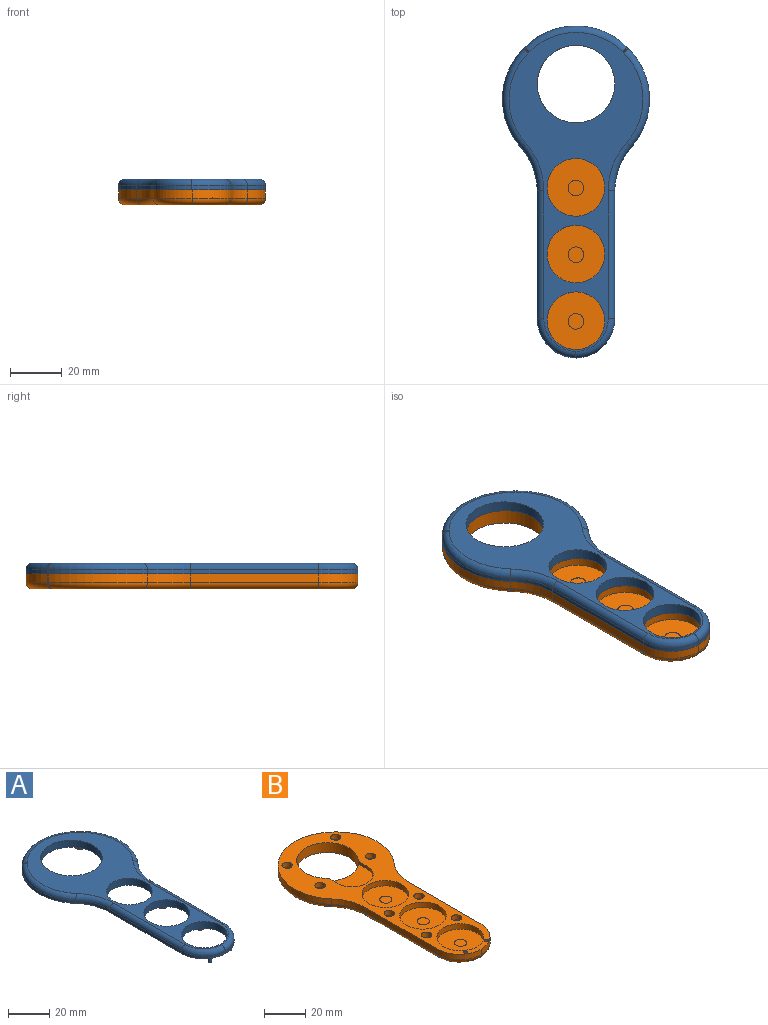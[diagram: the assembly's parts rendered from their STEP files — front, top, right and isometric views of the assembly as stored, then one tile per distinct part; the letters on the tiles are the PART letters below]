
ASSEMBLY  parts=2 mates=1
PART A: 48 faces, bbox 61.5x132x7.2 mm
  f0: plane 1.64x0.49mm, normal (0.71,0.71,0), area 1.1mm2, adj f5,f6,f8,f40
  f1: plane 1.64x0.49mm, normal (-0.71,0.71,0), area 1.1mm2, adj f5,f6,f7,f37
  f2: plane 49.38x1.64mm, normal (-1,0,0), area 80.7mm2, adj f5,f9,f12,f43
  f3: plane 49.38x1.64mm, normal (1,0,0), area 80.7mm2, adj f5,f10,f11,f46
  f4: plane 123.34x51.77mm, normal (0,0,1), area 1996.3mm2, adj f13,f14,f15,f16,f37,f38,f39,f40
  f5: plane 128.43x56.85mm, normal (0,0,-1), area 2639.4mm2, adj f0,f1,f2,f3,f6,f7,f8,f9
  f6: cylinder r=27.94mm len=39.51mm, axis (0,0,-1), area 71.8mm2, adj f0,f1,f5,f38
  f7: cylinder r=27.94mm len=38.29mm, axis (0,0,-1), area 69mm2, adj f1,f5,f9,f39
  f8: cylinder r=27.94mm len=38.29mm, axis (0,0,-1), area 69mm2, adj f0,f5,f10,f42
  f9: cylinder r=25.4mm len=16.85mm, axis (0,0,-1), area 30.1mm2, adj f2,f5,f7,f41
  f10: cylinder r=25.4mm len=16.85mm, axis (0,0,-1), area 30.1mm2, adj f3,f5,f8,f44
  f11: cylinder r=15.24mm len=15.24mm, axis (0,0,-1), area 38.7mm2, adj f3,f5,f12,f47
  f12: cylinder r=15.24mm len=15.24mm, axis (0,0,-1), area 38.7mm2, adj f2,f5,f11,f45
  f13: cylinder r=15mm len=30mm, axis (0,0,1), area 393.5mm2, adj f4,f5
  f14: cylinder r=11.15mm len=22.3mm, axis (0,0,1), area 292.5mm2, adj f4,f5
  f15: cylinder r=11.15mm len=22.3mm, axis (0,0,1), area 292.5mm2, adj f4,f5
  f16: cylinder r=11.15mm len=22.3mm, axis (0,0,1), area 292.5mm2, adj f4,f5
  f17: cylinder r=2.25mm len=4.5mm, axis (0,0,1), area 42.4mm2, adj f5,f18
  f18: plane 4.5x4.5mm, normal (0,0,-1), area 15.9mm2, adj f17
  f19: cylinder r=2.25mm len=4.5mm, axis (0,0,1), area 42.4mm2, adj f5,f20
  f20: plane 4.5x4.5mm, normal (0,0,-1), area 15.9mm2, adj f19
  f21: cylinder r=2.25mm len=4.5mm, axis (0,0,1), area 42.4mm2, adj f5,f22
  f22: plane 4.5x4.5mm, normal (0,0,-1), area 15.9mm2, adj f21
  f23: cylinder r=2.25mm len=4.5mm, axis (0,0,1), area 42.4mm2, adj f5,f24
  f24: plane 4.5x4.5mm, normal (0,0,-1), area 15.9mm2, adj f23
  f25: cylinder r=2.25mm len=4.5mm, axis (0,0,1), area 42.4mm2, adj f5,f26
  f26: plane 4.5x4.5mm, normal (0,0,-1), area 15.9mm2, adj f25
  f27: cylinder r=2.25mm len=4.5mm, axis (0,0,1), area 42.4mm2, adj f5,f28
  f28: plane 4.5x4.5mm, normal (0,0,-1), area 15.9mm2, adj f27
  f29: cylinder r=2.25mm len=4.5mm, axis (0,0,1), area 42.4mm2, adj f5,f30
  f30: plane 4.5x4.5mm, normal (0,0,-1), area 15.9mm2, adj f29
  f31: cylinder r=2.25mm len=4.5mm, axis (0,0,1), area 42.4mm2, adj f5,f32
  f32: plane 4.5x4.5mm, normal (0,0,-1), area 15.9mm2, adj f31
  f33: cylinder r=0.75mm len=3mm, axis (0,0,1), area 14.1mm2, adj f5,f34
  f34: plane 1.5x1.5mm, normal (0,0,-1), area 1.8mm2, adj f33
  f35: cylinder r=0.75mm len=3mm, axis (0,0,1), area 14.1mm2, adj f5,f36
  f36: plane 1.5x1.5mm, normal (0,0,-1), area 1.8mm2, adj f35
  f37: cylinder r=2.54mm len=2.54mm, axis (0.71,0.71,0), area 2.7mm2, adj f1,f4,f38,f39
  f38: torus R=25.4mm, axis (0,0,1), area 169.3mm2, adj f4,f6,f37,f40
  f39: torus R=25.4mm, axis (0,0,1), area 162.8mm2, adj f4,f7,f37,f41
  f40: cylinder r=2.54mm len=2.54mm, axis (0.71,-0.71,0), area 2.7mm2, adj f0,f4,f38,f42
  f41: torus R=27.94mm, axis (0,0,1), area 76.2mm2, adj f4,f9,f39,f43
  f42: torus R=25.4mm, axis (0,0,1), area 162.8mm2, adj f4,f8,f40,f44
  f43: cylinder r=2.54mm len=49.38mm, axis (0,1,0), area 197mm2, adj f2,f4,f41,f45
  f44: torus R=27.94mm, axis (0,0,1), area 76.2mm2, adj f4,f10,f42,f46
  f45: torus R=12.7mm, axis (0,0,1), area 88.7mm2, adj f4,f12,f43,f47
  f46: cylinder r=2.54mm len=49.38mm, axis (0,-1,0), area 197mm2, adj f3,f4,f44,f47
  f47: torus R=12.7mm, axis (0,0,1), area 88.7mm2, adj f4,f11,f45,f46
PART B: 63 faces, bbox 61.5x132x5.8 mm
  f0: cylinder r=15mm len=30mm, axis (0,0,1), area 512.2mm2, adj f1,f6,f26,f28,f29
  f1: plane 128.43x56.85mm, normal (0,0,1), area 2326.2mm2, adj f0,f2,f3,f4,f5,f7,f8,f9
  f2: plane 3.29x0.49mm, normal (0.71,0.71,0), area 2.3mm2, adj f1,f7,f9,f58
  f3: plane 3.29x0.49mm, normal (-0.71,0.71,0), area 2.3mm2, adj f1,f7,f8,f62
  f4: plane 49.38x3.29mm, normal (-1,0,0), area 162.2mm2, adj f1,f10,f13,f57
  f5: plane 49.38x3.29mm, normal (1,0,0), area 162.2mm2, adj f1,f11,f12,f52
  f6: plane 123.34x51.77mm, normal (0,0,-1), area 3168mm2, adj f0,f52,f53,f54,f55,f56,f57,f58
  f7: cylinder r=27.94mm len=39.51mm, axis (0,0,-1), area 144.2mm2, adj f1,f2,f3,f60
  f8: cylinder r=27.94mm len=38.29mm, axis (0,0,-1), area 138.7mm2, adj f1,f3,f10,f61
  f9: cylinder r=27.94mm len=38.29mm, axis (0,0,-1), area 138.7mm2, adj f1,f2,f11,f56
  f10: cylinder r=25.4mm len=16.85mm, axis (0,0,-1), area 60.5mm2, adj f1,f4,f8,f59
  f11: cylinder r=25.4mm len=16.85mm, axis (0,0,-1), area 60.5mm2, adj f1,f5,f9,f54
  f12: cylinder r=15.24mm len=15.24mm, axis (0,0,-1), area 77.9mm2, adj f1,f5,f13,f53
  f13: cylinder r=15.24mm len=15.24mm, axis (0,0,-1), area 77.9mm2, adj f1,f4,f12,f55
  f14: cylinder r=11.4mm len=22.8mm, axis (0,0,1), area 231mm2, adj f1,f15
  f15: plane 22.8x22.8mm, normal (0,0,1), area 380mm2, adj f14,f24
  f16: cylinder r=11.4mm len=22.8mm, axis (0,0,1), area 231mm2, adj f1,f17
  f17: plane 22.8x22.8mm, normal (0,0,1), area 380mm2, adj f16,f22
  f18: cylinder r=11.4mm len=22.8mm, axis (0,0,1), area 231mm2, adj f1,f19
  f19: plane 22.8x22.8mm, normal (0,0,1), area 380mm2, adj f18,f20
  f20: cylinder r=3mm len=6mm, axis (0,0,1), area 0.9mm2, adj f19,f21
  f21: plane 6x6mm, normal (0,0,1), area 28.3mm2, adj f20
  f22: cylinder r=3mm len=6mm, axis (0,0,1), area 0.9mm2, adj f17,f23
  f23: plane 6x6mm, normal (0,0,1), area 28.3mm2, adj f22
  f24: cylinder r=3mm len=6mm, axis (0,0,1), area 0.9mm2, adj f15,f25
  f25: plane 6x6mm, normal (0,0,1), area 28.3mm2, adj f24
  f26: plane 6.14x1.65mm, normal (1,0,0), area 10.1mm2, adj f0,f1,f29,f30
  f27: plane 1.65x0.68mm, normal (0,1,0), area 1.1mm2, adj f1,f29,f30,f31
  f28: plane 6.14x1.65mm, normal (-1,0,0), area 10.1mm2, adj f0,f1,f29,f31
  f29: plane 20.3x15.96mm, normal (0,0,1), area 227.5mm2, adj f0,f26,f27,f28,f30,f31
  f30: cylinder r=9.81mm len=9.81mm, axis (0,0,-1), area 25.4mm2, adj f1,f26,f27,f29
  f31: cylinder r=9.81mm len=9.81mm, axis (0,0,1), area 25.4mm2, adj f1,f27,f28,f29
  f32: cylinder r=2.5mm len=5mm, axis (0,0,1), area 47.1mm2, adj f1,f33
  f33: plane 5x5mm, normal (0,0,1), area 19.6mm2, adj f32
  f34: cylinder r=2.5mm len=5mm, axis (0,0,1), area 47.1mm2, adj f1,f35
  f35: plane 5x5mm, normal (0,0,1), area 19.6mm2, adj f34
  f36: cylinder r=2.5mm len=5mm, axis (0,0,1), area 47.1mm2, adj f1,f37
  f37: plane 5x5mm, normal (0,0,1), area 19.6mm2, adj f36
  f38: cylinder r=2.5mm len=5mm, axis (0,0,1), area 47.1mm2, adj f1,f39
  f39: plane 5x5mm, normal (0,0,1), area 19.6mm2, adj f38
  f40: cylinder r=2.5mm len=5mm, axis (0,0,1), area 47.1mm2, adj f1,f41
  f41: plane 5x5mm, normal (0,0,1), area 19.6mm2, adj f40
  f42: cylinder r=2.5mm len=5mm, axis (0,0,1), area 47.1mm2, adj f1,f43
  f43: plane 5x5mm, normal (0,0,1), area 19.6mm2, adj f42
  f44: cylinder r=2.5mm len=5mm, axis (0,0,1), area 47.1mm2, adj f1,f45
  f45: plane 5x5mm, normal (0,0,1), area 19.6mm2, adj f44
  f46: cylinder r=1mm len=3mm, axis (0,0,1), area 18.8mm2, adj f1,f47
  f47: plane 2x2mm, normal (0,0,1), area 3.1mm2, adj f46
  f48: cylinder r=1mm len=3mm, axis (0,0,1), area 18.8mm2, adj f1,f49
  f49: plane 2x2mm, normal (0,0,1), area 3.1mm2, adj f48
  f50: cylinder r=2.5mm len=5mm, axis (0,0,1), area 47.1mm2, adj f1,f51
  f51: plane 5x5mm, normal (0,0,1), area 19.6mm2, adj f50
  f52: cylinder r=2.54mm len=49.38mm, axis (0,1,0), area 197mm2, adj f5,f6,f53,f54
  f53: torus R=12.7mm, axis (0,0,1), area 88.7mm2, adj f6,f12,f52,f55
  f54: torus R=27.94mm, axis (0,0,1), area 76.2mm2, adj f6,f11,f52,f56
  f55: torus R=12.7mm, axis (0,0,1), area 88.7mm2, adj f6,f13,f53,f57
  f56: torus R=25.4mm, axis (0,0,1), area 162.8mm2, adj f6,f9,f54,f58
  f57: cylinder r=2.54mm len=49.38mm, axis (0,-1,0), area 197mm2, adj f4,f6,f55,f59
  f58: cylinder r=2.54mm len=2.54mm, axis (-0.71,0.71,0), area 2.7mm2, adj f2,f6,f56,f60
  f59: torus R=27.94mm, axis (0,0,1), area 76.2mm2, adj f6,f10,f57,f61
  f60: torus R=25.4mm, axis (0,0,1), area 169.3mm2, adj f6,f7,f58,f62
  f61: torus R=25.4mm, axis (0,0,1), area 162.8mm2, adj f6,f8,f59,f62
  f62: cylinder r=2.54mm len=2.54mm, axis (-0.71,-0.71,0), area 2.7mm2, adj f3,f6,f60,f61
PLACE A t=(-74.97,-43.58,48.29)mm
PLACE B t=(-74.97,-43.58,42.47)mm
MATE fastened B.f32 <-> A.f23  axis (0,0,1) through (-92.39,-21.75,48.29)mm
